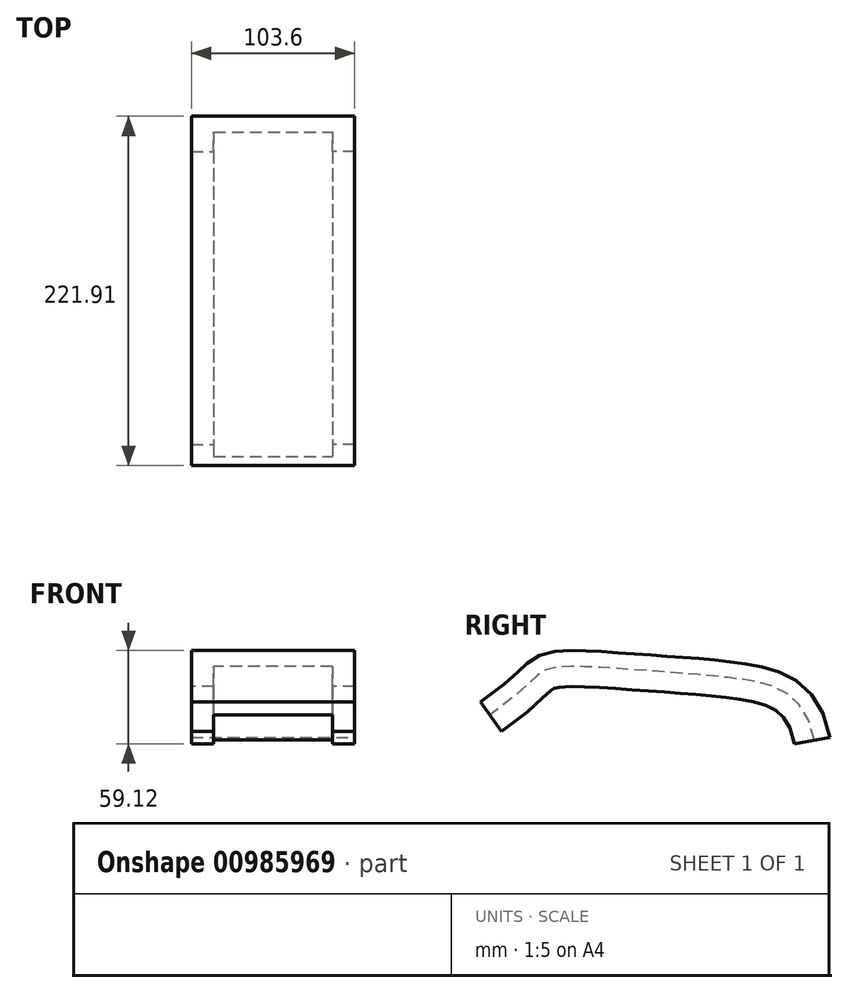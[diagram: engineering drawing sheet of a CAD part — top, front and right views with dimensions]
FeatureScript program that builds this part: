
annotation { "Feature Type Name" : "Feature", "Feature Type Description" : "" }
export const myFeature = defineFeature(function(context is Context, id is Id, definition is map)
    precondition{}
    {
        {
            var Q0;
            Q0=qCreatedBy(makeId("Right.planeOp"),FACE);
            var sketch = newSketch(context, id + "F0", { "sketchPlane" : qUnion([Q0])});
            skFitSpline(sketch, "E0", {"points": [v(-50.75, 0) * mm, v(-12.62, 29.32) * mm, v(40, 28.01) * mm, v(106.35, 22.1) * mm, v(150, -13.75) * mm], "startDerivative": vector(395.53, 282.6) * mm, "endDerivative": vector(60.78, -344.34) * mm});
            skSolve(sketch);
        }
        {
            var Q0;
            Q0=qCreatedBy(makeId("Front.planeOp"),FACE);
            var sketch = newSketch(context, id + "F1", { "sketchPlane" : qUnion([Q0])});
            skLineSegment(sketch, "E1", {"start": v(0, 43.73) * mm, "end": v(37.41, 43.73) * mm});
            skLineSegment(sketch, "E2", {"start": v(37.41, 43.73) * mm, "end": v(51.8, 43.73) * mm});
            skLineSegment(sketch, "E3", {"start": v(51.8, 43.73) * mm, "end": v(51.8, 20.86) * mm});
            skLineSegment(sketch, "E4", {"start": v(51.8, 20.86) * mm, "end": v(37.7, 20.86) * mm});
            skLineSegment(sketch, "E5", {"start": v(37.7, 20.86) * mm, "end": v(37.7, 33.64) * mm});
            skLineSegment(sketch, "E6", {"start": v(37.7, 33.64) * mm, "end": v(0, 33.64) * mm});
            skLineSegment(sketch, "E7.MirrorCS", {"start": v(0, 43.73) * mm, "end": v(-37.41, 43.73) * mm});
            skLineSegment(sketch, "E8.MirrorCS", {"start": v(-37.41, 43.73) * mm, "end": v(-51.8, 43.73) * mm});
            skLineSegment(sketch, "E9.MirrorCS", {"start": v(-51.8, 43.73) * mm, "end": v(-51.8, 20.86) * mm});
            skLineSegment(sketch, "E10.MirrorCS", {"start": v(-51.8, 20.86) * mm, "end": v(-37.7, 20.86) * mm});
            skLineSegment(sketch, "E11.MirrorCS", {"start": v(-37.7, 20.86) * mm, "end": v(-37.7, 33.64) * mm});
            skLineSegment(sketch, "E12.MirrorCS", {"start": v(-37.7, 33.64) * mm, "end": v(0, 33.64) * mm});
            skSolve(sketch);
        }
        {
            var Q0;
            Q0=makeQuery(id+"F1.imprint","IMPRINT",FACE,{"disambiguationData":[TD([[makeQuery(id+"F1.imprint","IMPRINT",EDGE,{"derivedFrom":sQuery(id+"F1.wireOp",EDGE,"E1")}),-1.0]])]});
            var Q1;
            Q1=sQuery(id+"F0.wireOp",EDGE,"E0");
            sweep(context, id + "F2", {"profiles" : qUnion([Q0]), "path" : qUnion([Q1])});
        }
    });
